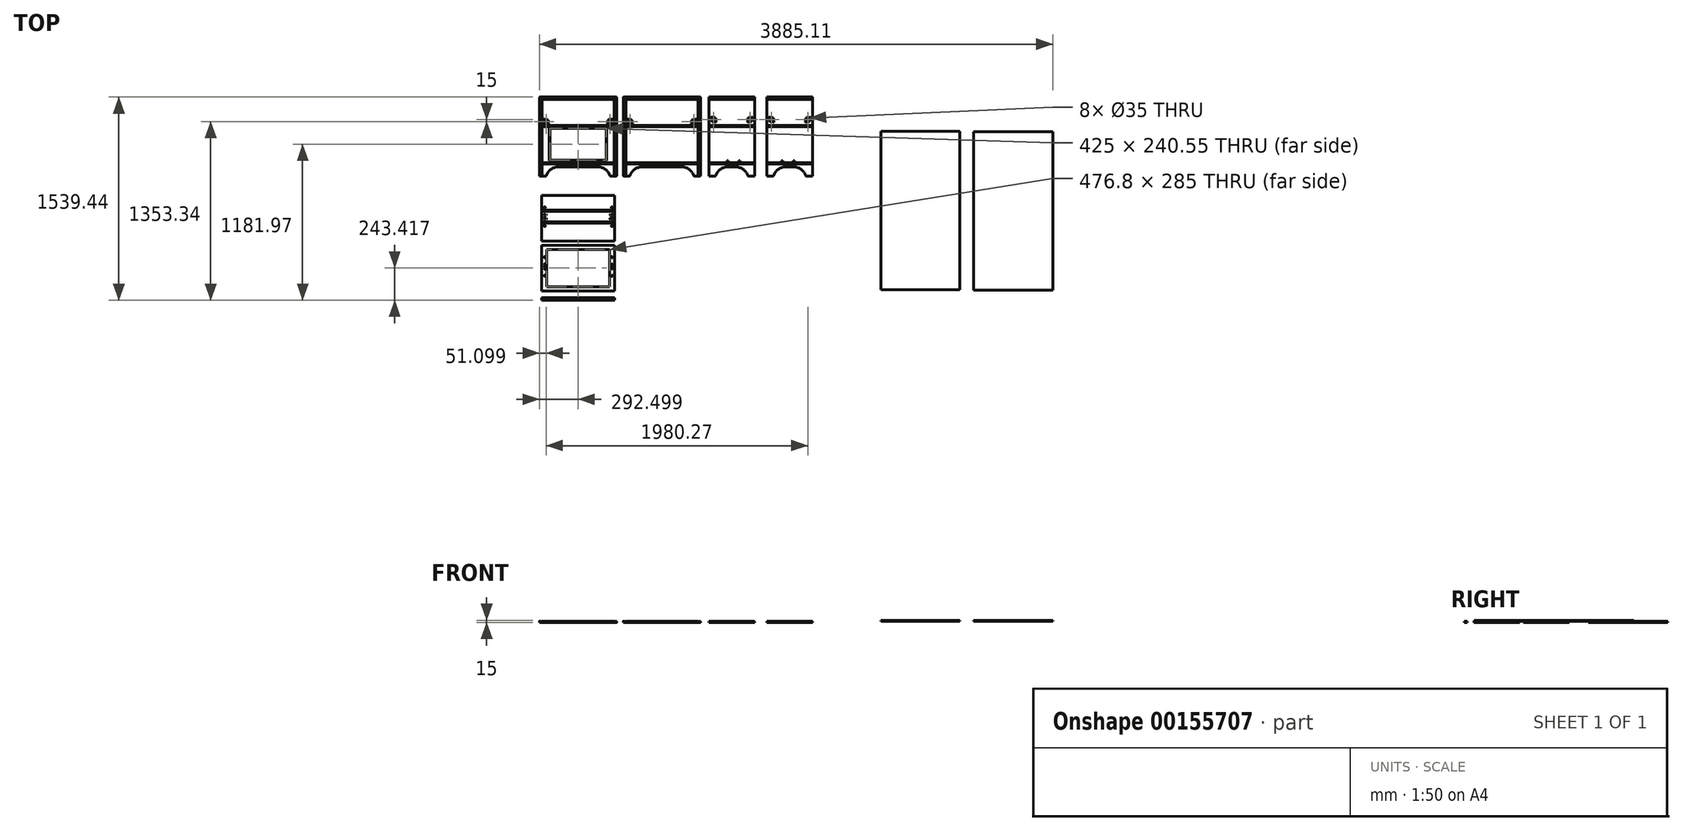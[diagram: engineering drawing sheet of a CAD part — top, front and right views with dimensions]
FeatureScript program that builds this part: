
annotation { "Feature Type Name" : "Feature", "Feature Type Description" : "" }
export const myFeature = defineFeature(function(context is Context, id is Id, definition is map)
    precondition{}
    {
        {
            var Q0;
            Q0=qCreatedBy(makeId("Top.planeOp"),FACE);
            var sketch = newSketch(context, id + "F0", { "sketchPlane" : qUnion([Q0])});
            skLineSegment(sketch, "E0", {"start": v(-123.83, 435.25) * mm, "end": v(-123.83, 505.5) * mm});
            skLineSegment(sketch, "E1", {"start": v(-123.83, 505.5) * mm, "end": v(361.17, 505.5) * mm});
            skLineSegment(sketch, "E2", {"start": v(361.17, 505.5) * mm, "end": v(361.17, 435.25) * mm});
            skLineSegment(sketch, "E3", {"start": v(361.17, 435.25) * mm, "end": v(411.17, 435.25) * mm});
            skLineSegment(sketch, "E4", {"start": v(-173.83, 435.25) * mm, "end": v(-123.83, 435.25) * mm});
            skLineSegment(sketch, "E5", {"start": v(-173.83, 435.25) * mm, "end": v(-173.83, 1035.25) * mm});
            skLineSegment(sketch, "E6", {"start": v(-173.83, 1035.25) * mm, "end": v(411.17, 1035.25) * mm});
            skLineSegment(sketch, "E7", {"start": v(411.17, 1035.25) * mm, "end": v(411.17, 435.25) * mm});
            skLineSegment(sketch, "E8", {"start": v(460.22, 1035.25) * mm, "end": v(1045.22, 1035.25) * mm});
            skLineSegment(sketch, "E9", {"start": v(1045.22, 1035.25) * mm, "end": v(1045.22, 435.25) * mm});
            skLineSegment(sketch, "E10", {"start": v(1045.22, 435.25) * mm, "end": v(995.22, 435.25) * mm});
            skLineSegment(sketch, "E11", {"start": v(995.22, 435.25) * mm, "end": v(995.22, 505.5) * mm});
            skLineSegment(sketch, "E12", {"start": v(995.22, 505.5) * mm, "end": v(510.22, 505.5) * mm});
            skLineSegment(sketch, "E13", {"start": v(510.22, 505.5) * mm, "end": v(510.22, 435.25) * mm});
            skLineSegment(sketch, "E14", {"start": v(510.22, 435.25) * mm, "end": v(460.22, 435.25) * mm});
            skLineSegment(sketch, "E15", {"start": v(460.22, 435.25) * mm, "end": v(460.22, 1035.25) * mm});
            skLineSegment(sketch, "E16", {"start": v(118.67, 1035.25) * mm, "end": v(118.67, 876.87) * mm, "construction": true});
            skLineSegment(sketch, "E17", {"start": v(118.67, 876.87) * mm, "end": v(118.67, 826.87) * mm, "construction": true});
            skLineSegment(sketch, "E18", {"start": v(118.67, 826.87) * mm, "end": v(118.67, 798.05) * mm, "construction": true});
            skLineSegment(sketch, "E19", {"start": v(118.67, 798.05) * mm, "end": v(118.67, 557.5) * mm, "construction": true});
            skLineSegment(sketch, "E20", {"start": v(118.67, 557.5) * mm, "end": v(118.67, 505.5) * mm, "construction": true});
            skLineSegment(sketch, "E21.bottom", {"start": v(26.17, 876.87) * mm, "end": v(211.17, 876.87) * mm});
            skLineSegment(sketch, "E21.top", {"start": v(26.17, 826.87) * mm, "end": v(211.17, 826.87) * mm});
            skLineSegment(sketch, "E21.left", {"start": v(26.17, 876.87) * mm, "end": v(26.17, 826.87) * mm});
            skLineSegment(sketch, "E21.right", {"start": v(211.17, 876.87) * mm, "end": v(211.17, 826.87) * mm});
            skLineSegment(sketch, "E22.bottom", {"start": v(-93.83, 798.05) * mm, "end": v(331.17, 798.05) * mm});
            skLineSegment(sketch, "E22.top", {"start": v(-93.83, 557.5) * mm, "end": v(331.17, 557.5) * mm});
            skLineSegment(sketch, "E22.left", {"start": v(-93.83, 798.05) * mm, "end": v(-93.83, 557.5) * mm});
            skLineSegment(sketch, "E22.right", {"start": v(331.17, 798.05) * mm, "end": v(331.17, 557.5) * mm});
            skLineSegment(sketch, "E23", {"start": v(26.17, 851.87) * mm, "end": v(-173.83, 851.87) * mm, "construction": true});
            skLineSegment(sketch, "E24", {"start": v(-93.83, 677.78) * mm, "end": v(-173.83, 677.78) * mm, "construction": true});
            skLineSegment(sketch, "E25", {"start": v(1109.16, 1035.25) * mm, "end": v(1454.16, 1035.25) * mm});
            skLineSegment(sketch, "E26", {"start": v(1454.16, 1035.25) * mm, "end": v(1454.16, 435.25) * mm});
            skLineSegment(sketch, "E27", {"start": v(1454.16, 435.25) * mm, "end": v(1404.16, 435.25) * mm});
            skLineSegment(sketch, "E28", {"start": v(1404.16, 435.25) * mm, "end": v(1404.16, 505.5) * mm});
            skLineSegment(sketch, "E29", {"start": v(1404.16, 505.5) * mm, "end": v(1159.16, 505.5) * mm});
            skLineSegment(sketch, "E30", {"start": v(1159.16, 505.5) * mm, "end": v(1159.16, 435.25) * mm});
            skLineSegment(sketch, "E31", {"start": v(1159.16, 435.25) * mm, "end": v(1109.16, 435.25) * mm});
            skLineSegment(sketch, "E32", {"start": v(1109.16, 435.25) * mm, "end": v(1109.16, 1035.25) * mm});
            skLineSegment(sketch, "E33", {"start": v(-163.83, 435.25) * mm, "end": v(-163.83, 1035.25) * mm});
            skLineSegment(sketch, "E34", {"start": v(-154.73, 435.25) * mm, "end": v(-154.73, 1035.25) * mm});
            skLineSegment(sketch, "E35", {"start": v(401.17, 435.25) * mm, "end": v(401.17, 1035.25) * mm});
            skLineSegment(sketch, "E36", {"start": v(392.07, 435.25) * mm, "end": v(392.07, 1035.25) * mm});
            skLineSegment(sketch, "E37", {"start": v(-154.73, 905.25) * mm, "end": v(392.07, 905.25) * mm});
            skLineSegment(sketch, "E38", {"start": v(392.07, 896.15) * mm, "end": v(-154.73, 896.15) * mm});
            skLineSegment(sketch, "E39", {"start": v(-154.73, 820.15) * mm, "end": v(392.07, 820.15) * mm});
            skLineSegment(sketch, "E40", {"start": v(392.07, 811.05) * mm, "end": v(-154.73, 811.05) * mm});
            skLineSegment(sketch, "E41", {"start": v(-154.73, 536.05) * mm, "end": v(392.07, 536.05) * mm});
            skLineSegment(sketch, "E42", {"start": v(392.07, 526.95) * mm, "end": v(-154.73, 526.95) * mm});
            skLineSegment(sketch, "E43", {"start": v(71.2, 905.25) * mm, "end": v(71.2, 1035.25) * mm, "construction": true});
            skLineSegment(sketch, "E44", {"start": v(71.36, 811.05) * mm, "end": v(71.36, 798.05) * mm, "construction": true});
            skLineSegment(sketch, "E45", {"start": v(27.92, 557.5) * mm, "end": v(27.92, 536.05) * mm, "construction": true});
            skLineSegment(sketch, "E46", {"start": v(29.17, 526.95) * mm, "end": v(29.17, 505.5) * mm, "construction": true});
            skLineSegment(sketch, "E47", {"start": v(470.22, 435.25) * mm, "end": v(470.22, 1035.25) * mm});
            skLineSegment(sketch, "E48", {"start": v(479.32, 435.25) * mm, "end": v(479.32, 1035.25) * mm});
            skLineSegment(sketch, "E49", {"start": v(1026.12, 435.25) * mm, "end": v(1026.12, 1035.25) * mm});
            skLineSegment(sketch, "E50", {"start": v(1035.22, 435.25) * mm, "end": v(1035.22, 1035.25) * mm});
            skLineSegment(sketch, "E51", {"start": v(479.32, 905.25) * mm, "end": v(1026.12, 905.25) * mm});
            skLineSegment(sketch, "E52", {"start": v(1026.12, 896.15) * mm, "end": v(479.32, 896.15) * mm});
            skLineSegment(sketch, "E53", {"start": v(479.32, 820.15) * mm, "end": v(1026.12, 820.15) * mm});
            skLineSegment(sketch, "E54", {"start": v(1026.12, 811.05) * mm, "end": v(479.32, 811.05) * mm});
            skLineSegment(sketch, "E55", {"start": v(479.32, 536.05) * mm, "end": v(1026.12, 536.05) * mm});
            skLineSegment(sketch, "E56", {"start": v(1026.12, 526.95) * mm, "end": v(479.32, 526.95) * mm});
            skLineSegment(sketch, "E57", {"start": v(-1640.99, 1035.25) * mm, "end": v(2090.02, 1035.25) * mm, "construction": true});
            skLineSegment(sketch, "E58", {"start": v(2090.02, 820.15) * mm, "end": v(-1631.04, 820.15) * mm, "construction": true});
            skLineSegment(sketch, "E59", {"start": v(-1631.04, 536.05) * mm, "end": v(2077.59, 536.05) * mm, "construction": true});
            skLineSegment(sketch, "E60", {"start": v(-795.13, 905.25) * mm, "end": v(2085.73, 905.25) * mm, "construction": true});
            skLineSegment(sketch, "E61", {"start": v(-1656.92, 811.05) * mm, "end": v(2077.22, 811.05) * mm, "construction": true});
            skLineSegment(sketch, "E62", {"start": v(2079.96, 526.95) * mm, "end": v(-1667.36, 526.95) * mm, "construction": true});
            skLineSegment(sketch, "E63", {"start": v(-1685.91, 896.15) * mm, "end": v(2079.86, 896.15) * mm, "construction": true});
            skLineSegment(sketch, "E64", {"start": v(1109.16, 536.05) * mm, "end": v(1454.16, 536.05) * mm});
            skLineSegment(sketch, "E65", {"start": v(1454.16, 526.95) * mm, "end": v(1109.16, 526.95) * mm});
            skLineSegment(sketch, "E66", {"start": v(1109.16, 820.15) * mm, "end": v(1454.16, 820.15) * mm});
            skLineSegment(sketch, "E67", {"start": v(1454.16, 811.05) * mm, "end": v(1109.16, 811.05) * mm});
            skLineSegment(sketch, "E68", {"start": v(1109.16, 905.25) * mm, "end": v(1454.16, 905.25) * mm});
            skLineSegment(sketch, "E69", {"start": v(1454.16, 896.15) * mm, "end": v(1109.16, 896.15) * mm});
            skLineSegment(sketch, "E70", {"start": v(-157.73, 320.51) * mm, "end": v(-157.73, -755.2) * mm, "construction": true});
            skLineSegment(sketch, "E71", {"start": v(395.07, 320.51) * mm, "end": v(395.07, -1181.01) * mm, "construction": true});
            skLineSegment(sketch, "E72.bottom", {"start": v(-157.73, 288.42) * mm, "end": v(395.07, 288.42) * mm});
            skLineSegment(sketch, "E72.top", {"start": v(-157.73, -56.58) * mm, "end": v(395.07, -56.58) * mm});
            skLineSegment(sketch, "E72.left", {"start": v(-157.73, 288.42) * mm, "end": v(-157.73, -56.58) * mm});
            skLineSegment(sketch, "E72.right", {"start": v(395.07, 288.42) * mm, "end": v(395.07, -56.58) * mm});
            skLineSegment(sketch, "E73.bottom", {"start": v(-157.73, -88.27) * mm, "end": v(395.07, -88.27) * mm});
            skLineSegment(sketch, "E73.top", {"start": v(-157.73, -433.27) * mm, "end": v(395.07, -433.27) * mm});
            skLineSegment(sketch, "E73.left", {"start": v(-157.73, -88.27) * mm, "end": v(-157.73, -433.27) * mm});
            skLineSegment(sketch, "E73.right", {"start": v(395.07, -88.27) * mm, "end": v(395.07, -433.27) * mm});
            skLineSegment(sketch, "E74.bottom", {"start": v(-119.73, -118.27) * mm, "end": v(357.07, -118.27) * mm});
            skLineSegment(sketch, "E74.top", {"start": v(-119.73, -403.27) * mm, "end": v(357.07, -403.27) * mm});
            skLineSegment(sketch, "E74.left", {"start": v(-119.73, -118.27) * mm, "end": v(-119.73, -403.27) * mm});
            skLineSegment(sketch, "E74.right", {"start": v(357.07, -118.27) * mm, "end": v(357.07, -403.27) * mm});
            skLineSegment(sketch, "E75", {"start": v(-157.73, -260.77) * mm, "end": v(-119.73, -260.77) * mm, "construction": true});
            skLineSegment(sketch, "E76", {"start": v(118.67, -88.27) * mm, "end": v(118.67, -118.27) * mm, "construction": true});
            skLineSegment(sketch, "E77", {"start": v(395.07, -260.77) * mm, "end": v(357.07, -260.77) * mm, "construction": true});
            skLineSegment(sketch, "E78", {"start": v(118.67, -433.27) * mm, "end": v(118.67, -403.27) * mm, "construction": true});
            skLineSegment(sketch, "E79", {"start": v(-154.73, 435.25) * mm, "end": v(-154.73, 320.51) * mm, "construction": true});
            skLineSegment(sketch, "E80", {"start": v(-154.73, 320.51) * mm, "end": v(392.07, 320.51) * mm, "construction": true});
            skLineSegment(sketch, "E81", {"start": v(392.07, 320.51) * mm, "end": v(392.07, 435.25) * mm, "construction": true});
            skLineSegment(sketch, "E82", {"start": v(-154.73, 320.51) * mm, "end": v(-157.73, 320.51) * mm, "construction": true});
            skLineSegment(sketch, "E83", {"start": v(392.07, 320.51) * mm, "end": v(395.07, 320.51) * mm, "construction": true});
            skPoint(sketch, "E84.startSnap0", {"position": v(118.67, -118.27) * mm});
            skCircle(sketch, "E85", {"center": v(132.27, 128.42) * mm, "radius": 27.3 * mm});
            skLineSegment(sketch, "E86", {"start": v(132.27, 128.42) * mm, "end": v(-157.73, 128.42) * mm, "construction": true});
            skLineSegment(sketch, "E87", {"start": v(132.27, 128.42) * mm, "end": v(132.27, -56.58) * mm, "construction": true});
            skLineSegment(sketch, "E88", {"start": v(-368.37, 1025.25) * mm, "end": v(2135.5, 1025.25) * mm, "construction": true});
            skLineSegment(sketch, "E89", {"start": v(2105.89, 1016.15) * mm, "end": v(-364.93, 1016.15) * mm, "construction": true});
            skLineSegment(sketch, "E90", {"start": v(-154.73, 1025.25) * mm, "end": v(392.07, 1025.25) * mm});
            skLineSegment(sketch, "E91", {"start": v(392.07, 1016.15) * mm, "end": v(-154.73, 1016.15) * mm});
            skLineSegment(sketch, "E92", {"start": v(479.32, 1025.25) * mm, "end": v(1026.12, 1025.25) * mm});
            skLineSegment(sketch, "E93", {"start": v(1026.12, 1016.15) * mm, "end": v(479.32, 1016.15) * mm});
            skLineSegment(sketch, "E94", {"start": v(1109.16, 1025.25) * mm, "end": v(1454.16, 1025.25) * mm});
            skLineSegment(sketch, "E95", {"start": v(1454.16, 1016.15) * mm, "end": v(1109.16, 1016.15) * mm});
            skLineSegment(sketch, "E96.bottom", {"start": v(-98.83, 803.05) * mm, "end": v(336.17, 803.05) * mm});
            skLineSegment(sketch, "E96.top", {"start": v(-98.83, 552.5) * mm, "end": v(336.17, 552.5) * mm});
            skLineSegment(sketch, "E96.left", {"start": v(-98.83, 803.05) * mm, "end": v(-98.83, 552.5) * mm});
            skLineSegment(sketch, "E96.right", {"start": v(336.17, 803.05) * mm, "end": v(336.17, 552.5) * mm});
            skLineSegment(sketch, "E97", {"start": v(331.17, 798.05) * mm, "end": v(336.17, 803.05) * mm, "construction": true});
            skLineSegment(sketch, "E98", {"start": v(331.17, 557.5) * mm, "end": v(336.17, 552.5) * mm, "construction": true});
            skLineSegment(sketch, "E99", {"start": v(-93.83, 557.5) * mm, "end": v(-98.83, 552.5) * mm, "construction": true});
            skLineSegment(sketch, "E100", {"start": v(-93.83, 798.05) * mm, "end": v(-98.83, 803.05) * mm, "construction": true});
            skLineSegment(sketch, "E101", {"start": v(92.3, 798.05) * mm, "end": v(92.3, 803.05) * mm, "construction": true});
            skLineSegment(sketch, "E102", {"start": v(-84.43, 128.42) * mm, "end": v(-84.43, 168.42) * mm, "construction": true});
            skLineSegment(sketch, "E103", {"start": v(-84.43, 128.42) * mm, "end": v(-84.43, 88.42) * mm, "construction": true});
            skLineSegment(sketch, "E104", {"start": v(-157.73, 168.42) * mm, "end": v(395.07, 168.42) * mm});
            skLineSegment(sketch, "E105", {"start": v(-157.73, 88.42) * mm, "end": v(395.07, 88.42) * mm});
            skLineSegment(sketch, "E106", {"start": v(-157.73, 177.52) * mm, "end": v(395.07, 177.52) * mm});
            skLineSegment(sketch, "E107", {"start": v(-157.73, 79.32) * mm, "end": v(395.07, 79.32) * mm});
            skLineSegment(sketch, "E108", {"start": v(-157.73, -484.19) * mm, "end": v(395.07, -484.19) * mm});
            skLineSegment(sketch, "E109", {"start": v(-157.73, -484.19) * mm, "end": v(-157.73, -504.19) * mm});
            skLineSegment(sketch, "E110", {"start": v(-157.73, -504.19) * mm, "end": v(395.07, -504.19) * mm});
            skLineSegment(sketch, "E111", {"start": v(395.07, -504.19) * mm, "end": v(395.07, -484.19) * mm});
            skLineSegment(sketch, "E112", {"start": v(1294.16, 573.28) * mm, "end": v(1254.16, 573.28) * mm, "construction": true});
            skLineSegment(sketch, "E113", {"start": v(1294.16, 573.28) * mm, "end": v(1334.16, 573.28) * mm, "construction": true});
            skLineSegment(sketch, "E114", {"start": v(1254.16, 573.28) * mm, "end": v(1254.16, 536.05) * mm, "construction": true});
            skLineSegment(sketch, "E115", {"start": v(1334.16, 573.28) * mm, "end": v(1334.16, 536.05) * mm, "construction": true});
            skLineSegment(sketch, "E116", {"start": v(1254.16, 553.15) * mm, "end": v(1245.06, 553.15) * mm});
            skLineSegment(sketch, "E117", {"start": v(1245.06, 553.15) * mm, "end": v(1245.06, 536.05) * mm});
            skLineSegment(sketch, "E118", {"start": v(1254.16, 553.15) * mm, "end": v(1254.16, 536.05) * mm});
            skLineSegment(sketch, "E119", {"start": v(1334.16, 553.15) * mm, "end": v(1343.26, 553.15) * mm});
            skLineSegment(sketch, "E120", {"start": v(1343.26, 553.15) * mm, "end": v(1343.26, 536.05) * mm});
            skLineSegment(sketch, "E121", {"start": v(1334.16, 553.15) * mm, "end": v(1334.16, 536.05) * mm});
            skLineSegment(sketch, "E122", {"start": v(1294.16, 573.28) * mm, "end": v(1294.16, 536.05) * mm, "construction": true});
            skLineSegment(sketch, "E123", {"start": v(1294.16, 573.28) * mm, "end": v(1454.16, 573.28) * mm, "construction": true});
            skLineSegment(sketch, "E124", {"start": v(1294.16, 573.28) * mm, "end": v(1109.16, 573.28) * mm, "construction": true});
            skLineSegment(sketch, "E125", {"start": v(1547.54, 1035.25) * mm, "end": v(1892.54, 1035.25) * mm});
            skLineSegment(sketch, "E126", {"start": v(1892.54, 1035.25) * mm, "end": v(1892.54, 435.25) * mm});
            skLineSegment(sketch, "E127", {"start": v(1892.54, 435.25) * mm, "end": v(1842.54, 435.25) * mm});
            skLineSegment(sketch, "E128", {"start": v(1842.54, 435.25) * mm, "end": v(1842.54, 505.5) * mm});
            skLineSegment(sketch, "E129", {"start": v(1842.54, 505.5) * mm, "end": v(1597.54, 505.5) * mm});
            skLineSegment(sketch, "E130", {"start": v(1597.54, 505.5) * mm, "end": v(1597.54, 435.25) * mm});
            skLineSegment(sketch, "E131", {"start": v(1597.54, 435.25) * mm, "end": v(1547.54, 435.25) * mm});
            skLineSegment(sketch, "E132", {"start": v(1547.54, 435.25) * mm, "end": v(1547.54, 1035.25) * mm});
            skLineSegment(sketch, "E133", {"start": v(1547.54, 536.05) * mm, "end": v(1892.54, 536.05) * mm});
            skLineSegment(sketch, "E134", {"start": v(1892.54, 526.95) * mm, "end": v(1547.54, 526.95) * mm});
            skLineSegment(sketch, "E135", {"start": v(1547.54, 820.15) * mm, "end": v(1892.54, 820.15) * mm});
            skLineSegment(sketch, "E136", {"start": v(1892.54, 811.05) * mm, "end": v(1547.54, 811.05) * mm});
            skLineSegment(sketch, "E137", {"start": v(1547.54, 905.25) * mm, "end": v(1892.54, 905.25) * mm});
            skLineSegment(sketch, "E138", {"start": v(1892.54, 896.15) * mm, "end": v(1547.54, 896.15) * mm});
            skLineSegment(sketch, "E139", {"start": v(1547.54, 1025.25) * mm, "end": v(1892.54, 1025.25) * mm});
            skLineSegment(sketch, "E140", {"start": v(1892.54, 1016.15) * mm, "end": v(1547.54, 1016.15) * mm});
            skLineSegment(sketch, "E141", {"start": v(1707.54, 567.75) * mm, "end": v(1667.54, 567.75) * mm, "construction": true});
            skLineSegment(sketch, "E142", {"start": v(1707.54, 567.75) * mm, "end": v(1747.54, 567.75) * mm, "construction": true});
            skLineSegment(sketch, "E143", {"start": v(1667.54, 567.75) * mm, "end": v(1667.54, 536.05) * mm, "construction": true});
            skLineSegment(sketch, "E144", {"start": v(1747.54, 567.75) * mm, "end": v(1747.54, 536.05) * mm, "construction": true});
            skLineSegment(sketch, "E145", {"start": v(1667.54, 553.15) * mm, "end": v(1658.44, 553.15) * mm});
            skLineSegment(sketch, "E146", {"start": v(1658.44, 553.15) * mm, "end": v(1658.44, 536.05) * mm});
            skLineSegment(sketch, "E147", {"start": v(1667.54, 553.15) * mm, "end": v(1667.54, 536.05) * mm});
            skLineSegment(sketch, "E148", {"start": v(1747.54, 553.15) * mm, "end": v(1756.64, 553.15) * mm});
            skLineSegment(sketch, "E149", {"start": v(1756.64, 553.15) * mm, "end": v(1756.64, 536.05) * mm});
            skLineSegment(sketch, "E150", {"start": v(1747.54, 553.15) * mm, "end": v(1747.54, 536.05) * mm});
            skLineSegment(sketch, "E151", {"start": v(1707.54, 567.75) * mm, "end": v(1707.54, 536.05) * mm, "construction": true});
            skLineSegment(sketch, "E152", {"start": v(1707.54, 567.75) * mm, "end": v(1892.54, 567.75) * mm, "construction": true});
            skLineSegment(sketch, "E153", {"start": v(1707.54, 567.75) * mm, "end": v(1547.54, 567.75) * mm, "construction": true});
            skSolve(sketch);
        }
        {
            var Q0;
            {var subQ0=sQuery(id+"F0.wireOp",EDGE,"E54");Q0=makeQuery(id+"F0.imprint","IMPRINT",FACE,{"disambiguationData":[TD([[makeQuery(id+"F0.imprint","IMPRINT",EDGE,{"derivedFrom":subQ0}),1.0]])]});}
            var Q1;
            Q1=makeQuery(id+"F0.imprint","IMPRINT",FACE,{"disambiguationData":[TD([[makeQuery(id+"F0.imprint","IMPRINT",EDGE,{"derivedFrom":sQuery(id+"F0.wireOp",EDGE,"E22.top")}),-1.0]])]});
            var Q2;
            {var subQ0=sQuery(id+"F0.wireOp",EDGE,"E9");Q2=makeQuery(id+"F0.imprint","IMPRINT",FACE,{"disambiguationData":[TD([[makeQuery(id+"F0.imprint","IMPRINT",EDGE,{"derivedFrom":subQ0}),-1.0]])]});}
            var Q3;
            {var subQ0=sQuery(id+"F0.wireOp",EDGE,"E51");Q3=makeQuery(id+"F0.imprint","IMPRINT",FACE,{"disambiguationData":[TD([[makeQuery(id+"F0.imprint","IMPRINT",EDGE,{"derivedFrom":subQ0}),1.0]])]});}
            var Q4;
            {var subQ0=sQuery(id+"F0.wireOp",EDGE,"E66");Q4=makeQuery(id+"F0.imprint","IMPRINT",FACE,{"disambiguationData":[TD([[makeQuery(id+"F0.imprint","IMPRINT",EDGE,{"derivedFrom":subQ0}),1.0]])]});}
            var Q5;
            Q5=makeQuery(id+"F0.imprint","IMPRINT",FACE,{"disambiguationData":[TD([[makeQuery(id+"F0.imprint","IMPRINT",EDGE,{"derivedFrom":sQuery(id+"F0.wireOp",EDGE,"E73.bottom")}),-1.0]])]});
            var Q6;
            {var subQ0=sQuery(id+"F0.wireOp",EDGE,"E27");Q6=makeQuery(id+"F0.imprint","IMPRINT",FACE,{"disambiguationData":[TD([[makeQuery(id+"F0.imprint","IMPRINT",EDGE,{"derivedFrom":subQ0}),-1.0]])]});}
            var Q7;
            {var subQ0=sQuery(id+"F0.wireOp",EDGE,"E25");Q7=makeQuery(id+"F0.imprint","IMPRINT",FACE,{"disambiguationData":[TD([[makeQuery(id+"F0.imprint","IMPRINT",EDGE,{"derivedFrom":subQ0}),-1.0]])]});}
            var Q8;
            {var subQ0=sQuery(id+"F0.wireOp",EDGE,"E72.bottom");Q8=makeQuery(id+"F0.imprint","IMPRINT",FACE,{"disambiguationData":[TD([[makeQuery(id+"F0.imprint","IMPRINT",EDGE,{"derivedFrom":subQ0}),-1.0]])]});}
            var Q9;
            {var subQ0=sQuery(id+"F0.wireOp",EDGE,"E37");Q9=makeQuery(id+"F0.imprint","IMPRINT",FACE,{"disambiguationData":[TD([[makeQuery(id+"F0.imprint","IMPRINT",EDGE,{"derivedFrom":subQ0}),1.0]])]});}
            var Q10;
            {var subQ6=sQuery(id+"F0.wireOp",EDGE,"E67");Q10=makeQuery(id+"F0.imprint","IMPRINT",FACE,{"disambiguationData":[TD([[makeQuery(id+"F0.imprint","IMPRINT",EDGE,{"derivedFrom":subQ6}),1.0]])]});}
            var Q11;
            {var subQ6=sQuery(id+"F0.wireOp",EDGE,"E0");Q11=makeQuery(id+"F0.imprint","IMPRINT",FACE,{"disambiguationData":[TD([[makeQuery(id+"F0.imprint","IMPRINT",EDGE,{"derivedFrom":subQ6}),1.0]])]});}
            var Q12;
            {var subQ5=sQuery(id+"F0.wireOp",EDGE,"E21.bottom");Q12=makeQuery(id+"F0.imprint","IMPRINT",FACE,{"disambiguationData":[TD([[makeQuery(id+"F0.imprint","IMPRINT",EDGE,{"derivedFrom":subQ5}),1.0]])]});}
            var Q13;
            {var subQ0=sQuery(id+"F0.wireOp",EDGE,"E52");Q13=makeQuery(id+"F0.imprint","IMPRINT",FACE,{"disambiguationData":[TD([[makeQuery(id+"F0.imprint","IMPRINT",EDGE,{"derivedFrom":subQ0}),1.0]])]});}
            var Q14;
            {var subQ5=sQuery(id+"F0.wireOp",EDGE,"E11");Q14=makeQuery(id+"F0.imprint","IMPRINT",FACE,{"disambiguationData":[TD([[makeQuery(id+"F0.imprint","IMPRINT",EDGE,{"derivedFrom":subQ5}),-1.0]])]});}
            var Q15;
            {var subQ3=sQuery(id+"F0.wireOp",EDGE,"E33");Q15=makeQuery(id+"F0.imprint","IMPRINT",FACE,{"disambiguationData":[TD([[makeQuery(id+"F0.imprint","IMPRINT",EDGE,{"derivedFrom":subQ3}),-1.0]])]});}
            var Q16;
            {var subQ0=sQuery(id+"F0.wireOp",EDGE,"E55");Q16=makeQuery(id+"F0.imprint","IMPRINT",FACE,{"disambiguationData":[TD([[makeQuery(id+"F0.imprint","IMPRINT",EDGE,{"derivedFrom":subQ0}),-1.0]])]});}
            var Q17;
            {var subQ11=sQuery(id+"F0.wireOp",EDGE,"E35");Q17=makeQuery(id+"F0.imprint","IMPRINT",FACE,{"disambiguationData":[TD([[makeQuery(id+"F0.imprint","IMPRINT",EDGE,{"derivedFrom":subQ11}),1.0]])]});}
            var Q18;
            {var subQ0=sQuery(id+"F0.wireOp",EDGE,"E37");Q18=makeQuery(id+"F0.imprint","IMPRINT",FACE,{"disambiguationData":[TD([[makeQuery(id+"F0.imprint","IMPRINT",EDGE,{"derivedFrom":subQ0}),-1.0]])]});}
            var Q19;
            {var subQ0=sQuery(id+"F0.wireOp",EDGE,"E66");Q19=makeQuery(id+"F0.imprint","IMPRINT",FACE,{"disambiguationData":[TD([[makeQuery(id+"F0.imprint","IMPRINT",EDGE,{"derivedFrom":subQ0}),-1.0]])]});}
            var Q20;
            {var subQ0=sQuery(id+"F0.wireOp",EDGE,"E68");Q20=makeQuery(id+"F0.imprint","IMPRINT",FACE,{"disambiguationData":[TD([[makeQuery(id+"F0.imprint","IMPRINT",EDGE,{"derivedFrom":subQ0}),-1.0]])]});}
            var Q21;
            {var subQ0=sQuery(id+"F0.wireOp",EDGE,"E15");Q21=makeQuery(id+"F0.imprint","IMPRINT",FACE,{"disambiguationData":[TD([[makeQuery(id+"F0.imprint","IMPRINT",EDGE,{"derivedFrom":subQ0}),-1.0]])]});}
            var Q22;
            {var subQ0=sQuery(id+"F0.wireOp",EDGE,"E5");Q22=makeQuery(id+"F0.imprint","IMPRINT",FACE,{"disambiguationData":[TD([[makeQuery(id+"F0.imprint","IMPRINT",EDGE,{"derivedFrom":subQ0}),-1.0]])]});}
            var Q23;
            {var subQ0=sQuery(id+"F0.wireOp",EDGE,"E7");Q23=makeQuery(id+"F0.imprint","IMPRINT",FACE,{"disambiguationData":[TD([[makeQuery(id+"F0.imprint","IMPRINT",EDGE,{"derivedFrom":subQ0}),-1.0]])]});}
            var Q24;
            {var subQ5=sQuery(id+"F0.wireOp",EDGE,"E65");Q24=makeQuery(id+"F0.imprint","IMPRINT",FACE,{"disambiguationData":[TD([[makeQuery(id+"F0.imprint","IMPRINT",EDGE,{"derivedFrom":subQ5}),-1.0]])]});}
            var Q25;
            {var subQ0=sQuery(id+"F0.wireOp",EDGE,"E39");var subQ1=sQuery(id+"F0.wireOp",EDGE,"E21.left");var subQ2=makeQuery(id+"F0.imprint","INTERSECT",VERTEX,{"derivedFrom":[subQ1,subQ0]});Q25=makeQuery(id+"F0.imprint","IMPRINT",FACE,{"disambiguationData":[TD([[makeQuery(id+"F0.imprint","IMPRINT",EDGE,{"disambiguationData":[TD([[subQ2,-1.0]])],"derivedFrom":subQ1}),1.0]])]});}
            var Q26;
            {var subQ0=sQuery(id+"F0.wireOp",EDGE,"E39");var subQ1=sQuery(id+"F0.wireOp",EDGE,"E21.left");var subQ2=makeQuery(id+"F0.imprint","INTERSECT",VERTEX,{"derivedFrom":[subQ1,subQ0]});Q26=makeQuery(id+"F0.imprint","IMPRINT",FACE,{"disambiguationData":[TD([[makeQuery(id+"F0.imprint","IMPRINT",EDGE,{"disambiguationData":[TD([[subQ2,-1.0]])],"derivedFrom":subQ1}),-1.0]])]});}
            var Q27;
            {var subQ0=sQuery(id+"F0.wireOp",EDGE,"E39");var subQ1=sQuery(id+"F0.wireOp",EDGE,"E21.right");var subQ2=makeQuery(id+"F0.imprint","INTERSECT",VERTEX,{"derivedFrom":[subQ1,subQ0]});Q27=makeQuery(id+"F0.imprint","IMPRINT",FACE,{"disambiguationData":[TD([[makeQuery(id+"F0.imprint","IMPRINT",EDGE,{"disambiguationData":[TD([[subQ2,-1.0]])],"derivedFrom":subQ1}),1.0]])]});}
            var Q28;
            {var subQ0=sQuery(id+"F0.wireOp",EDGE,"E51");Q28=makeQuery(id+"F0.imprint","IMPRINT",FACE,{"disambiguationData":[TD([[makeQuery(id+"F0.imprint","IMPRINT",EDGE,{"derivedFrom":subQ0}),-1.0]])]});}
            var Q29;
            {var subQ0=sQuery(id+"F0.wireOp",EDGE,"E41");Q29=makeQuery(id+"F0.imprint","IMPRINT",FACE,{"disambiguationData":[TD([[makeQuery(id+"F0.imprint","IMPRINT",EDGE,{"derivedFrom":subQ0}),-1.0]])]});}
            var Q30;
            {var subQ0=sQuery(id+"F0.wireOp",EDGE,"E53");Q30=makeQuery(id+"F0.imprint","IMPRINT",FACE,{"disambiguationData":[TD([[makeQuery(id+"F0.imprint","IMPRINT",EDGE,{"derivedFrom":subQ0}),-1.0]])]});}
            var Q31;
            {var subQ11=sQuery(id+"F0.wireOp",EDGE,"E47");Q31=makeQuery(id+"F0.imprint","IMPRINT",FACE,{"disambiguationData":[TD([[makeQuery(id+"F0.imprint","IMPRINT",EDGE,{"derivedFrom":subQ11}),-1.0]])]});}
            var Q32;
            {var subQ5=sQuery(id+"F0.wireOp",EDGE,"E50");Q32=makeQuery(id+"F0.imprint","IMPRINT",FACE,{"disambiguationData":[TD([[makeQuery(id+"F0.imprint","IMPRINT",EDGE,{"derivedFrom":subQ5}),1.0]])]});}
            var Q33;
            {var subQ0=sQuery(id+"F0.wireOp",EDGE,"E90");Q33=makeQuery(id+"F0.imprint","IMPRINT",FACE,{"disambiguationData":[TD([[makeQuery(id+"F0.imprint","IMPRINT",EDGE,{"derivedFrom":subQ0}),-1.0]])]});}
            var Q34;
            {var subQ5=sQuery(id+"F0.wireOp",EDGE,"E90");Q34=makeQuery(id+"F0.imprint","IMPRINT",FACE,{"disambiguationData":[TD([[makeQuery(id+"F0.imprint","IMPRINT",EDGE,{"derivedFrom":subQ5}),1.0]])]});}
            var Q35;
            {var subQ5=sQuery(id+"F0.wireOp",EDGE,"E92");Q35=makeQuery(id+"F0.imprint","IMPRINT",FACE,{"disambiguationData":[TD([[makeQuery(id+"F0.imprint","IMPRINT",EDGE,{"derivedFrom":subQ5}),1.0]])]});}
            var Q36;
            {var subQ0=sQuery(id+"F0.wireOp",EDGE,"E92");Q36=makeQuery(id+"F0.imprint","IMPRINT",FACE,{"disambiguationData":[TD([[makeQuery(id+"F0.imprint","IMPRINT",EDGE,{"derivedFrom":subQ0}),-1.0]])]});}
            var Q37;
            {var subQ0=sQuery(id+"F0.wireOp",EDGE,"E94");Q37=makeQuery(id+"F0.imprint","IMPRINT",FACE,{"disambiguationData":[TD([[makeQuery(id+"F0.imprint","IMPRINT",EDGE,{"derivedFrom":subQ0}),-1.0]])]});}
            var Q38;
            {var subQ0=sQuery(id+"F0.wireOp",EDGE,"E68");Q38=makeQuery(id+"F0.imprint","IMPRINT",FACE,{"disambiguationData":[TD([[makeQuery(id+"F0.imprint","IMPRINT",EDGE,{"derivedFrom":subQ0}),1.0]])]});}
            var Q39;
            {var subQ0=sQuery(id+"F0.wireOp",EDGE,"E21.bottom");Q39=makeQuery(id+"F0.imprint","IMPRINT",FACE,{"disambiguationData":[TD([[makeQuery(id+"F0.imprint","IMPRINT",EDGE,{"derivedFrom":subQ0}),-1.0]])]});}
            var Q40;
            {var subQ7=sQuery(id+"F0.wireOp",EDGE,"E41");Q40=makeQuery(id+"F0.imprint","IMPRINT",FACE,{"disambiguationData":[TD([[makeQuery(id+"F0.imprint","IMPRINT",EDGE,{"derivedFrom":subQ7}),1.0]])]});}
            var Q41;
            Q41=makeQuery(id+"F0.imprint","IMPRINT",FACE,{"disambiguationData":[TD([[makeQuery(id+"F0.imprint","IMPRINT",EDGE,{"derivedFrom":sQuery(id+"F0.wireOp",EDGE,"E85")}),1.0]])]});
            var Q42;
            Q42=makeQuery(id+"F0.imprint","IMPRINT",FACE,{"disambiguationData":[TD([[makeQuery(id+"F0.imprint","IMPRINT",EDGE,{"derivedFrom":sQuery(id+"F0.wireOp",EDGE,"E85")}),-1.0]])]});
            var Q43;
            {var subQ0=sQuery(id+"F0.wireOp",EDGE,"E72.top");Q43=makeQuery(id+"F0.imprint","IMPRINT",FACE,{"disambiguationData":[TD([[makeQuery(id+"F0.imprint","IMPRINT",EDGE,{"derivedFrom":subQ0}),1.0]])]});}
            var Q44;
            {var subQ0=sQuery(id+"F0.wireOp",EDGE,"E105");Q44=makeQuery(id+"F0.imprint","IMPRINT",FACE,{"disambiguationData":[TD([[makeQuery(id+"F0.imprint","IMPRINT",EDGE,{"derivedFrom":subQ0}),-1.0]])]});}
            var Q45;
            {var subQ0=sQuery(id+"F0.wireOp",EDGE,"E104");Q45=makeQuery(id+"F0.imprint","IMPRINT",FACE,{"disambiguationData":[TD([[makeQuery(id+"F0.imprint","IMPRINT",EDGE,{"derivedFrom":subQ0}),1.0]])]});}
            var Q46;
            Q46=makeQuery(id+"F0.imprint","IMPRINT",FACE,{"disambiguationData":[TD([[makeQuery(id+"F0.imprint","IMPRINT",EDGE,{"derivedFrom":sQuery(id+"F0.wireOp",EDGE,"E116")}),1.0]])]});
            var Q47;
            Q47=makeQuery(id+"F0.imprint","IMPRINT",FACE,{"disambiguationData":[TD([[makeQuery(id+"F0.imprint","IMPRINT",EDGE,{"derivedFrom":sQuery(id+"F0.wireOp",EDGE,"E119")}),-1.0]])]});
            var Q48;
            Q48=makeQuery(id+"F0.imprint","IMPRINT",FACE,{"disambiguationData":[TD([[makeQuery(id+"F0.imprint","IMPRINT",EDGE,{"derivedFrom":sQuery(id+"F0.wireOp",EDGE,"E108")}),-1.0]])]});
            var Q49;
            {var subQ5=sQuery(id+"F0.wireOp",EDGE,"E136");Q49=makeQuery(id+"F0.imprint","IMPRINT",FACE,{"disambiguationData":[TD([[makeQuery(id+"F0.imprint","IMPRINT",EDGE,{"derivedFrom":subQ5}),1.0]])]});}
            var Q50;
            {var subQ0=sQuery(id+"F0.wireOp",EDGE,"E127");Q50=makeQuery(id+"F0.imprint","IMPRINT",FACE,{"disambiguationData":[TD([[makeQuery(id+"F0.imprint","IMPRINT",EDGE,{"derivedFrom":subQ0}),-1.0]])]});}
            var Q51;
            {var subQ0=sQuery(id+"F0.wireOp",EDGE,"E125");Q51=makeQuery(id+"F0.imprint","IMPRINT",FACE,{"disambiguationData":[TD([[makeQuery(id+"F0.imprint","IMPRINT",EDGE,{"derivedFrom":subQ0}),-1.0]])]});}
            var Q52;
            {var subQ0=sQuery(id+"F0.wireOp",EDGE,"E135");Q52=makeQuery(id+"F0.imprint","IMPRINT",FACE,{"disambiguationData":[TD([[makeQuery(id+"F0.imprint","IMPRINT",EDGE,{"derivedFrom":subQ0}),1.0]])]});}
            var Q53;
            {var subQ0=sQuery(id+"F0.wireOp",EDGE,"E137");Q53=makeQuery(id+"F0.imprint","IMPRINT",FACE,{"disambiguationData":[TD([[makeQuery(id+"F0.imprint","IMPRINT",EDGE,{"derivedFrom":subQ0}),1.0]])]});}
            var Q54;
            {var subQ0=sQuery(id+"F0.wireOp",EDGE,"E135");Q54=makeQuery(id+"F0.imprint","IMPRINT",FACE,{"disambiguationData":[TD([[makeQuery(id+"F0.imprint","IMPRINT",EDGE,{"derivedFrom":subQ0}),-1.0]])]});}
            var Q55;
            {var subQ5=sQuery(id+"F0.wireOp",EDGE,"E134");Q55=makeQuery(id+"F0.imprint","IMPRINT",FACE,{"disambiguationData":[TD([[makeQuery(id+"F0.imprint","IMPRINT",EDGE,{"derivedFrom":subQ5}),-1.0]])]});}
            var Q56;
            {var subQ0=sQuery(id+"F0.wireOp",EDGE,"E139");Q56=makeQuery(id+"F0.imprint","IMPRINT",FACE,{"disambiguationData":[TD([[makeQuery(id+"F0.imprint","IMPRINT",EDGE,{"derivedFrom":subQ0}),-1.0]])]});}
            var Q57;
            {var subQ0=sQuery(id+"F0.wireOp",EDGE,"E137");Q57=makeQuery(id+"F0.imprint","IMPRINT",FACE,{"disambiguationData":[TD([[makeQuery(id+"F0.imprint","IMPRINT",EDGE,{"derivedFrom":subQ0}),-1.0]])]});}
            var Q58;
            Q58=makeQuery(id+"F0.imprint","IMPRINT",FACE,{"disambiguationData":[TD([[makeQuery(id+"F0.imprint","IMPRINT",EDGE,{"derivedFrom":sQuery(id+"F0.wireOp",EDGE,"E145")}),1.0]])]});
            var Q59;
            Q59=makeQuery(id+"F0.imprint","IMPRINT",FACE,{"disambiguationData":[TD([[makeQuery(id+"F0.imprint","IMPRINT",EDGE,{"derivedFrom":sQuery(id+"F0.wireOp",EDGE,"E148")}),-1.0]])]});
            var Q60;
            {var subQ0=sQuery(id+"F0.wireOp",EDGE,"E39");Q60=makeQuery(id+"F0.imprint","IMPRINT",FACE,{"disambiguationData":[TD([[makeQuery(id+"F0.imprint","IMPRINT",EDGE,{"derivedFrom":subQ0}),-1.0]])]});}
            extrude(context, id + "F1", {"entities" : qUnion([Q0, Q1, Q2, Q3, Q4, Q5, Q6, Q7, Q8, Q9, Q10, Q11, Q12, Q13, Q14, Q15, Q16, Q17, Q18, Q19, Q20, Q21, Q22, Q23, Q24, Q25, Q26, Q27, Q28, Q29, Q30, Q31, Q32, Q33, Q34, Q35, Q36, Q37, Q38, Q39, Q40, Q41, Q42, Q43, Q44, Q45, Q46, Q47, Q48, Q49, Q50, Q51, Q52, Q53, Q54, Q55, Q56, Q57, Q58, Q59, Q60]), "oppositeDirection" : true, "depth" : 9 * mm});
        }
        {
            var Q0;
            {var subQ0=sQuery(id+"F0.wireOp",EDGE,"E39");Q0=makeQuery(id+"F0.imprint","IMPRINT",FACE,{"disambiguationData":[TD([[makeQuery(id+"F0.imprint","IMPRINT",EDGE,{"derivedFrom":subQ0}),-1.0]])]});}
            var Q1;
            {var subQ7=sQuery(id+"F0.wireOp",EDGE,"E33");Q1=makeQuery(id+"F0.imprint","IMPRINT",FACE,{"disambiguationData":[TD([[makeQuery(id+"F0.imprint","IMPRINT",EDGE,{"derivedFrom":subQ7}),-1.0]])]});}
            var Q2;
            {var subQ0=sQuery(id+"F0.wireOp",EDGE,"E41");Q2=makeQuery(id+"F0.imprint","IMPRINT",FACE,{"disambiguationData":[TD([[makeQuery(id+"F0.imprint","IMPRINT",EDGE,{"derivedFrom":subQ0}),-1.0]])]});}
            var Q3;
            {var subQ4=sQuery(id+"F0.wireOp",EDGE,"E35");Q3=makeQuery(id+"F0.imprint","IMPRINT",FACE,{"disambiguationData":[TD([[makeQuery(id+"F0.imprint","IMPRINT",EDGE,{"derivedFrom":subQ4}),1.0]])]});}
            var Q4;
            {var subQ0=sQuery(id+"F0.wireOp",EDGE,"E47");Q4=makeQuery(id+"F0.imprint","IMPRINT",FACE,{"disambiguationData":[TD([[makeQuery(id+"F0.imprint","IMPRINT",EDGE,{"derivedFrom":subQ0}),-1.0]])]});}
            var Q5;
            {var subQ0=sQuery(id+"F0.wireOp",EDGE,"E53");Q5=makeQuery(id+"F0.imprint","IMPRINT",FACE,{"disambiguationData":[TD([[makeQuery(id+"F0.imprint","IMPRINT",EDGE,{"derivedFrom":subQ0}),-1.0]])]});}
            var Q6;
            {var subQ0=sQuery(id+"F0.wireOp",EDGE,"E55");Q6=makeQuery(id+"F0.imprint","IMPRINT",FACE,{"disambiguationData":[TD([[makeQuery(id+"F0.imprint","IMPRINT",EDGE,{"derivedFrom":subQ0}),-1.0]])]});}
            var Q7;
            {var subQ3=sQuery(id+"F0.wireOp",EDGE,"E50");Q7=makeQuery(id+"F0.imprint","IMPRINT",FACE,{"disambiguationData":[TD([[makeQuery(id+"F0.imprint","IMPRINT",EDGE,{"derivedFrom":subQ3}),1.0]])]});}
            var Q8;
            {var subQ0=sQuery(id+"F0.wireOp",EDGE,"E66");Q8=makeQuery(id+"F0.imprint","IMPRINT",FACE,{"disambiguationData":[TD([[makeQuery(id+"F0.imprint","IMPRINT",EDGE,{"derivedFrom":subQ0}),-1.0]])]});}
            var Q9;
            {var subQ0=sQuery(id+"F0.wireOp",EDGE,"E64");Q9=makeQuery(id+"F0.imprint","IMPRINT",FACE,{"disambiguationData":[TD([[makeQuery(id+"F0.imprint","IMPRINT",EDGE,{"derivedFrom":subQ0}),-1.0]])]});}
            var Q10;
            {var subQ0=sQuery(id+"F0.wireOp",EDGE,"E90");Q10=makeQuery(id+"F0.imprint","IMPRINT",FACE,{"disambiguationData":[TD([[makeQuery(id+"F0.imprint","IMPRINT",EDGE,{"derivedFrom":subQ0}),-1.0]])]});}
            var Q11;
            {var subQ0=sQuery(id+"F0.wireOp",EDGE,"E92");Q11=makeQuery(id+"F0.imprint","IMPRINT",FACE,{"disambiguationData":[TD([[makeQuery(id+"F0.imprint","IMPRINT",EDGE,{"derivedFrom":subQ0}),-1.0]])]});}
            var Q12;
            {var subQ0=sQuery(id+"F0.wireOp",EDGE,"E94");Q12=makeQuery(id+"F0.imprint","IMPRINT",FACE,{"disambiguationData":[TD([[makeQuery(id+"F0.imprint","IMPRINT",EDGE,{"derivedFrom":subQ0}),-1.0]])]});}
            var Q13;
            Q13=makeQuery(id+"F0.imprint","IMPRINT",FACE,{"disambiguationData":[TD([[makeQuery(id+"F0.imprint","IMPRINT",EDGE,{"derivedFrom":sQuery(id+"F0.wireOp",EDGE,"E22.bottom")}),1.0]])]});
            var Q14;
            {var subQ0=sQuery(id+"F0.wireOp",EDGE,"E104");Q14=makeQuery(id+"F0.imprint","IMPRINT",FACE,{"disambiguationData":[TD([[makeQuery(id+"F0.imprint","IMPRINT",EDGE,{"derivedFrom":subQ0}),1.0]])]});}
            var Q15;
            {var subQ0=sQuery(id+"F0.wireOp",EDGE,"E105");Q15=makeQuery(id+"F0.imprint","IMPRINT",FACE,{"disambiguationData":[TD([[makeQuery(id+"F0.imprint","IMPRINT",EDGE,{"derivedFrom":subQ0}),-1.0]])]});}
            var Q16;
            Q16=makeQuery(id+"F0.imprint","IMPRINT",FACE,{"disambiguationData":[TD([[makeQuery(id+"F0.imprint","IMPRINT",EDGE,{"derivedFrom":sQuery(id+"F0.wireOp",EDGE,"E116")}),1.0]])]});
            var Q17;
            Q17=makeQuery(id+"F0.imprint","IMPRINT",FACE,{"disambiguationData":[TD([[makeQuery(id+"F0.imprint","IMPRINT",EDGE,{"derivedFrom":sQuery(id+"F0.wireOp",EDGE,"E119")}),-1.0]])]});
            var Q18;
            {var subQ5=sQuery(id+"F0.wireOp",EDGE,"E134");Q18=makeQuery(id+"F0.imprint","IMPRINT",FACE,{"disambiguationData":[TD([[makeQuery(id+"F0.imprint","IMPRINT",EDGE,{"derivedFrom":subQ5}),-1.0]])]});}
            var Q19;
            Q19=makeQuery(id+"F0.imprint","IMPRINT",FACE,{"disambiguationData":[TD([[makeQuery(id+"F0.imprint","IMPRINT",EDGE,{"derivedFrom":sQuery(id+"F0.wireOp",EDGE,"E145")}),1.0]])]});
            var Q20;
            Q20=makeQuery(id+"F0.imprint","IMPRINT",FACE,{"disambiguationData":[TD([[makeQuery(id+"F0.imprint","IMPRINT",EDGE,{"derivedFrom":sQuery(id+"F0.wireOp",EDGE,"E148")}),-1.0]])]});
            var Q21;
            {var subQ0=sQuery(id+"F0.wireOp",EDGE,"E135");Q21=makeQuery(id+"F0.imprint","IMPRINT",FACE,{"disambiguationData":[TD([[makeQuery(id+"F0.imprint","IMPRINT",EDGE,{"derivedFrom":subQ0}),-1.0]])]});}
            var Q22;
            {var subQ0=sQuery(id+"F0.wireOp",EDGE,"E139");Q22=makeQuery(id+"F0.imprint","IMPRINT",FACE,{"disambiguationData":[TD([[makeQuery(id+"F0.imprint","IMPRINT",EDGE,{"derivedFrom":subQ0}),-1.0]])]});}
            extrude(context, id + "F2", {"entities" : qUnion([Q0, Q1, Q2, Q3, Q4, Q5, Q6, Q7, Q8, Q9, Q10, Q11, Q12, Q13, Q14, Q15, Q16, Q17, Q18, Q19, Q20, Q21, Q22]), "operationType" : NewBodyOperationType.REMOVE, "oppositeDirection" : true, "depth" : 3 * mm});
        }
        {
            var Q0;
            Q0=qCreatedBy(makeId("Top.planeOp"),FACE);
            var sketch = newSketch(context, id + "F3", { "sketchPlane" : qUnion([Q0])});
            skLineSegment(sketch, "E154.0", {"start": v(-1685.91, 896.15) * mm, "end": v(2079.86, 896.15) * mm, "construction": true});
            skLineSegment(sketch, "E155", {"start": v(-249.8, 896.15) * mm, "end": v(-249.8, 864.15) * mm, "construction": true});
            skLineSegment(sketch, "E156", {"start": v(-249.8, 864.15) * mm, "end": v(-249.8, 849.15) * mm, "construction": true});
            skLineSegment(sketch, "E157", {"start": v(-249.8, 849.15) * mm, "end": v(2116.66, 849.15) * mm, "construction": true});
            skLineSegment(sketch, "E158.0", {"start": v(-154.73, 435.25) * mm, "end": v(-154.73, 1035.25) * mm, "construction": true});
            skLineSegment(sketch, "E159", {"start": v(-154.73, 778.4) * mm, "end": v(-122.73, 778.4) * mm, "construction": true});
            skLineSegment(sketch, "E160", {"start": v(-122.73, 778.4) * mm, "end": v(-122.73, 849.15) * mm, "construction": true});
            skCircle(sketch, "E161", {"center": v(-122.73, 849.15) * mm, "radius": 6 * mm});
            skCircle(sketch, "E162", {"center": v(-122.73, 849.15) * mm, "radius": 22.5 * mm, "construction": true});
            skLineSegment(sketch, "E163", {"start": v(-122.73, 808.5) * mm, "end": v(-122.73, 849.15) * mm, "construction": true});
            skLineSegment(sketch, "E164", {"start": v(-138.64, 865.06) * mm, "end": v(-122.73, 849.15) * mm, "construction": true});
            skLineSegment(sketch, "E165", {"start": v(-122.73, 849.15) * mm, "end": v(-106.82, 833.24) * mm, "construction": true});
            skCircle(sketch, "E166", {"center": v(-138.64, 865.06) * mm, "radius": 3.3 * mm});
            skCircle(sketch, "E167", {"center": v(-106.82, 833.24) * mm, "radius": 3.3 * mm});
            skLineSegment(sketch, "E168.0", {"start": v(392.07, 435.25) * mm, "end": v(392.07, 1035.25) * mm, "construction": true});
            skLineSegment(sketch, "E169", {"start": v(392.07, 833.43) * mm, "end": v(360.07, 833.43) * mm, "construction": true});
            skLineSegment(sketch, "E170", {"start": v(360.07, 833.43) * mm, "end": v(360.07, 849.15) * mm, "construction": true});
            skCircle(sketch, "E171", {"center": v(360.07, 849.15) * mm, "radius": 6 * mm});
            skCircle(sketch, "E172", {"center": v(360.07, 849.15) * mm, "radius": 22.5 * mm, "construction": true});
            skCircle(sketch, "E173", {"center": v(344.16, 833.24) * mm, "radius": 3.3 * mm});
            skCircle(sketch, "E174", {"center": v(375.98, 865.06) * mm, "radius": 3.3 * mm});
            skLineSegment(sketch, "E175", {"start": v(360.07, 849.15) * mm, "end": v(344.16, 833.24) * mm, "construction": true});
            skLineSegment(sketch, "E176", {"start": v(375.98, 865.06) * mm, "end": v(360.07, 849.15) * mm, "construction": true});
            skLineSegment(sketch, "E177", {"start": v(-138.64, 865.06) * mm, "end": v(-138.64, 849.15) * mm, "construction": true});
            skLineSegment(sketch, "E178", {"start": v(375.98, 865.06) * mm, "end": v(375.98, 849.15) * mm, "construction": true});
            skLineSegment(sketch, "E179.0", {"start": v(479.32, 435.25) * mm, "end": v(479.32, 1035.25) * mm, "construction": true});
            skLineSegment(sketch, "E180.0", {"start": v(1026.12, 435.25) * mm, "end": v(1026.12, 1035.25) * mm, "construction": true});
            skLineSegment(sketch, "E181", {"start": v(1112.16, 778.46) * mm, "end": v(1144.16, 778.46) * mm, "construction": true});
            skLineSegment(sketch, "E182", {"start": v(1144.16, 778.46) * mm, "end": v(1144.16, 864.15) * mm, "construction": true});
            skLineSegment(sketch, "E183", {"start": v(1451.16, 779.39) * mm, "end": v(1419.16, 779.39) * mm, "construction": true});
            skLineSegment(sketch, "E184", {"start": v(1419.16, 779.39) * mm, "end": v(1419.16, 864.15) * mm, "construction": true});
            skCircle(sketch, "E185", {"center": v(1144.16, 864.15) * mm, "radius": 6 * mm});
            skCircle(sketch, "E186", {"center": v(1419.16, 864.15) * mm, "radius": 6 * mm});
            skCircle(sketch, "E187", {"center": v(1144.16, 864.15) * mm, "radius": 22.5 * mm, "construction": true});
            skCircle(sketch, "E188", {"center": v(1160.07, 848.24) * mm, "radius": 3.3 * mm});
            skCircle(sketch, "E189", {"center": v(1128.25, 880.06) * mm, "radius": 3.3 * mm});
            skCircle(sketch, "E190", {"center": v(1419.16, 864.15) * mm, "radius": 22.5 * mm, "construction": true});
            skCircle(sketch, "E191", {"center": v(1435.07, 880.06) * mm, "radius": 3.3 * mm});
            skCircle(sketch, "E192", {"center": v(1403.25, 848.24) * mm, "radius": 3.3 * mm});
            skLineSegment(sketch, "E193", {"start": v(1160.07, 848.24) * mm, "end": v(1144.16, 864.15) * mm, "construction": true});
            skLineSegment(sketch, "E194", {"start": v(1144.16, 864.15) * mm, "end": v(1128.25, 880.06) * mm, "construction": true});
            skLineSegment(sketch, "E195", {"start": v(1435.07, 880.06) * mm, "end": v(1419.16, 864.15) * mm, "construction": true});
            skLineSegment(sketch, "E196", {"start": v(1419.16, 864.15) * mm, "end": v(1403.25, 848.24) * mm, "construction": true});
            skLineSegment(sketch, "E197.0", {"start": v(1454.16, 1035.25) * mm, "end": v(1454.16, 435.25) * mm, "construction": true});
            skLineSegment(sketch, "E198.0", {"start": v(1109.16, 435.25) * mm, "end": v(1109.16, 1035.25) * mm, "construction": true});
            skLineSegment(sketch, "E199", {"start": v(1451.16, 779.39) * mm, "end": v(1454.16, 779.39) * mm, "construction": true});
            skLineSegment(sketch, "E200", {"start": v(1109.16, 778.46) * mm, "end": v(1112.16, 778.46) * mm, "construction": true});
            skLineSegment(sketch, "E201", {"start": v(479.32, 777.65) * mm, "end": v(511.32, 777.65) * mm, "construction": true});
            skLineSegment(sketch, "E202", {"start": v(511.32, 777.65) * mm, "end": v(511.32, 849.15) * mm, "construction": true});
            skCircle(sketch, "E203", {"center": v(511.32, 849.15) * mm, "radius": 22.5 * mm, "construction": true});
            skCircle(sketch, "E204", {"center": v(495.41, 865.06) * mm, "radius": 3.3 * mm});
            skCircle(sketch, "E205", {"center": v(527.23, 833.24) * mm, "radius": 3.3 * mm});
            skCircle(sketch, "E206", {"center": v(511.32, 849.15) * mm, "radius": 6 * mm});
            skLineSegment(sketch, "E207", {"start": v(495.41, 865.06) * mm, "end": v(511.32, 849.15) * mm, "construction": true});
            skLineSegment(sketch, "E208", {"start": v(527.23, 833.24) * mm, "end": v(511.32, 849.15) * mm, "construction": true});
            skLineSegment(sketch, "E209", {"start": v(994.12, 820.6) * mm, "end": v(994.12, 849.15) * mm, "construction": true});
            skCircle(sketch, "E210", {"center": v(994.12, 849.15) * mm, "radius": 22.5 * mm, "construction": true});
            skCircle(sketch, "E211", {"center": v(1010.03, 865.06) * mm, "radius": 3.3 * mm});
            skCircle(sketch, "E212", {"center": v(978.21, 833.24) * mm, "radius": 3.3 * mm});
            skCircle(sketch, "E213", {"center": v(994.12, 849.15) * mm, "radius": 6 * mm});
            skLineSegment(sketch, "E214", {"start": v(1010.03, 865.06) * mm, "end": v(994.12, 849.15) * mm, "construction": true});
            skLineSegment(sketch, "E215", {"start": v(978.21, 833.24) * mm, "end": v(994.12, 849.15) * mm, "construction": true});
            skLineSegment(sketch, "E216", {"start": v(1010.03, 865.06) * mm, "end": v(1010.03, 849.15) * mm, "construction": true});
            skLineSegment(sketch, "E217", {"start": v(994.12, 820.6) * mm, "end": v(1026.12, 820.6) * mm, "construction": true});
            skLineSegment(sketch, "E218", {"start": v(-249.8, 864.15) * mm, "end": v(2099.82, 864.15) * mm, "construction": true});
            skCircle(sketch, "E219", {"center": v(-122.73, 849.15) * mm, "radius": 17.5 * mm});
            skCircle(sketch, "E220", {"center": v(360.07, 849.15) * mm, "radius": 17.5 * mm});
            skCircle(sketch, "E221", {"center": v(511.32, 849.15) * mm, "radius": 17.5 * mm});
            skCircle(sketch, "E222", {"center": v(994.12, 849.15) * mm, "radius": 17.5 * mm});
            skCircle(sketch, "E223", {"center": v(1144.16, 864.15) * mm, "radius": 17.5 * mm});
            skCircle(sketch, "E224", {"center": v(1419.16, 864.15) * mm, "radius": 17.5 * mm});
            skLineSegment(sketch, "E225", {"start": v(-157.73, 128.42) * mm, "end": v(395.07, 128.42) * mm, "construction": true});
            skLineSegment(sketch, "E226", {"start": v(-157.73, 128.42) * mm, "end": v(-134.73, 128.42) * mm, "construction": true});
            skLineSegment(sketch, "E227", {"start": v(-134.73, 128.42) * mm, "end": v(-134.73, 198.42) * mm, "construction": true});
            skLineSegment(sketch, "E228", {"start": v(-134.73, 128.42) * mm, "end": v(-134.73, 58.42) * mm, "construction": true});
            skLineSegment(sketch, "E229", {"start": v(395.07, 128.42) * mm, "end": v(375.07, 128.42) * mm, "construction": true});
            skLineSegment(sketch, "E230", {"start": v(375.07, 128.42) * mm, "end": v(375.07, 198.42) * mm, "construction": true});
            skLineSegment(sketch, "E231", {"start": v(375.07, 128.42) * mm, "end": v(375.07, 58.42) * mm, "construction": true});
            skCircle(sketch, "E232", {"center": v(-134.73, 198.42) * mm, "radius": 5 * mm});
            skCircle(sketch, "E233", {"center": v(-134.73, 58.42) * mm, "radius": 5 * mm});
            skCircle(sketch, "E234", {"center": v(375.07, 198.42) * mm, "radius": 5 * mm});
            skCircle(sketch, "E235", {"center": v(375.07, 58.42) * mm, "radius": 5 * mm});
            skLineSegment(sketch, "E236.0", {"start": v(395.07, -88.27) * mm, "end": v(395.07, -433.27) * mm, "construction": true});
            skLineSegment(sketch, "E237", {"start": v(403.63, -260.77) * mm, "end": v(-119.73, -260.77) * mm, "construction": true});
            skLineSegment(sketch, "E238.0", {"start": v(-157.73, -88.27) * mm, "end": v(-157.73, -433.27) * mm, "construction": true});
            skLineSegment(sketch, "E239", {"start": v(-134.73, 58.42) * mm, "end": v(-134.73, -435.33) * mm, "construction": true});
            skLineSegment(sketch, "E240", {"start": v(375.07, 58.42) * mm, "end": v(375.07, -442.17) * mm, "construction": true});
            skCircle(sketch, "E241", {"center": v(-134.73, -248.27) * mm, "radius": 70 * mm, "construction": true});
            skCircle(sketch, "E242", {"center": v(375.07, -248.27) * mm, "radius": 70 * mm, "construction": true});
            skCircle(sketch, "E243", {"center": v(-134.73, -178.27) * mm, "radius": 5 * mm});
            skPoint(sketch, "E243.centerSnap0", {"position": v(-134.73, -188.45) * mm});
            skCircle(sketch, "E244", {"center": v(-134.73, -318.27) * mm, "radius": 5 * mm});
            skCircle(sketch, "E245", {"center": v(375.07, -178.27) * mm, "radius": 5 * mm});
            skCircle(sketch, "E246", {"center": v(375.07, -318.27) * mm, "radius": 5 * mm});
            skLineSegment(sketch, "E247", {"start": v(-134.73, -248.27) * mm, "end": v(375.07, -248.27) * mm, "construction": true});
            skLineSegment(sketch, "E248.0", {"start": v(-157.73, -433.27) * mm, "end": v(395.07, -433.27) * mm, "construction": true});
            skLineSegment(sketch, "E249", {"start": v(174.89, -433.27) * mm, "end": v(174.89, -248.27) * mm, "construction": true});
            skCircle(sketch, "E250", {"center": v(375.07, 128.42) * mm, "radius": 18.25 * mm, "construction": true});
            skCircle(sketch, "E251", {"center": v(-134.73, 128.42) * mm, "radius": 18.25 * mm, "construction": true});
            skCircle(sketch, "E252", {"center": v(-134.73, -248.27) * mm, "radius": 18.25 * mm, "construction": true});
            skCircle(sketch, "E253", {"center": v(375.07, -248.27) * mm, "radius": 18.25 * mm, "construction": true});
            skCircle(sketch, "E254", {"center": v(-134.73, 128.42) * mm, "radius": 4.25 * mm});
            skCircle(sketch, "E255", {"center": v(375.07, 128.42) * mm, "radius": 4.25 * mm});
            skCircle(sketch, "E256", {"center": v(375.07, -248.27) * mm, "radius": 4.25 * mm});
            skCircle(sketch, "E257", {"center": v(-134.73, -248.27) * mm, "radius": 4.25 * mm});
            skCircle(sketch, "E258", {"center": v(-134.73, -230.02) * mm, "radius": 2.5 * mm});
            skCircle(sketch, "E259", {"center": v(-134.73, -266.52) * mm, "radius": 2.5 * mm});
            skCircle(sketch, "E260", {"center": v(375.07, -230.02) * mm, "radius": 2.5 * mm});
            skCircle(sketch, "E261", {"center": v(375.07, -266.52) * mm, "radius": 2.5 * mm});
            skCircle(sketch, "E262", {"center": v(375.07, 146.67) * mm, "radius": 2.5 * mm});
            skCircle(sketch, "E263", {"center": v(375.07, 110.17) * mm, "radius": 2.5 * mm});
            skCircle(sketch, "E264", {"center": v(-134.73, 146.67) * mm, "radius": 2.5 * mm});
            skCircle(sketch, "E265", {"center": v(-134.73, 110.17) * mm, "radius": 2.5 * mm});
            skCircle(sketch, "E266", {"center": v(-397.55, 636.07) * mm, "radius": 21.9 * mm, "construction": true});
            skLineSegment(sketch, "E267", {"start": v(-413.03, 651.56) * mm, "end": v(-382.06, 620.59) * mm, "construction": true});
            skLineSegment(sketch, "E268", {"start": v(-382.06, 651.56) * mm, "end": v(-413.03, 620.59) * mm, "construction": true});
            skCircle(sketch, "E269", {"center": v(-413.03, 651.56) * mm, "radius": 1.5 * mm});
            skCircle(sketch, "E270", {"center": v(-382.06, 651.56) * mm, "radius": 1.5 * mm});
            skCircle(sketch, "E271", {"center": v(-382.06, 620.59) * mm, "radius": 1.5 * mm});
            skCircle(sketch, "E272", {"center": v(-413.03, 620.59) * mm, "radius": 1.5 * mm});
            skLineSegment(sketch, "E273", {"start": v(-397.55, 657.97) * mm, "end": v(-397.55, 614.17) * mm, "construction": true});
            skCircle(sketch, "E274", {"center": v(360.07, 849.15) * mm, "radius": 21.9 * mm, "construction": true});
            skLineSegment(sketch, "E275", {"start": v(360.07, 871.05) * mm, "end": v(360.07, 827.25) * mm, "construction": true});
            skLineSegment(sketch, "E276", {"start": v(381.97, 849.15) * mm, "end": v(338.17, 849.15) * mm, "construction": true});
            skCircle(sketch, "E277", {"center": v(360.07, 871.05) * mm, "radius": 1.5 * mm});
            skCircle(sketch, "E278", {"center": v(381.97, 849.15) * mm, "radius": 1.5 * mm});
            skCircle(sketch, "E279", {"center": v(360.07, 827.25) * mm, "radius": 1.5 * mm});
            skCircle(sketch, "E280", {"center": v(338.17, 849.15) * mm, "radius": 1.5 * mm});
            skCircle(sketch, "E281", {"center": v(1144.16, 864.15) * mm, "radius": 21.9 * mm, "construction": true});
            skLineSegment(sketch, "E282", {"start": v(1144.16, 886.05) * mm, "end": v(1144.16, 842.25) * mm, "construction": true});
            skLineSegment(sketch, "E283", {"start": v(1166.06, 864.15) * mm, "end": v(1122.26, 864.15) * mm, "construction": true});
            skCircle(sketch, "E284", {"center": v(1144.16, 886.05) * mm, "radius": 1.5 * mm});
            skCircle(sketch, "E285", {"center": v(1166.06, 864.15) * mm, "radius": 1.5 * mm});
            skCircle(sketch, "E286", {"center": v(1144.16, 842.25) * mm, "radius": 1.5 * mm});
            skCircle(sketch, "E287", {"center": v(1122.26, 864.15) * mm, "radius": 1.5 * mm});
            skCircle(sketch, "E288", {"center": v(-134.73, 128.42) * mm, "radius": 21.9 * mm, "construction": true});
            skLineSegment(sketch, "E289", {"start": v(-150.22, 143.9) * mm, "end": v(-119.25, 112.93) * mm, "construction": true});
            skLineSegment(sketch, "E290", {"start": v(-119.25, 143.9) * mm, "end": v(-150.22, 112.93) * mm, "construction": true});
            skCircle(sketch, "E291", {"center": v(-150.22, 143.9) * mm, "radius": 1.5 * mm});
            skCircle(sketch, "E292", {"center": v(-119.25, 143.9) * mm, "radius": 1.5 * mm});
            skCircle(sketch, "E293", {"center": v(-119.25, 112.93) * mm, "radius": 1.5 * mm});
            skCircle(sketch, "E294", {"center": v(-150.22, 112.93) * mm, "radius": 1.5 * mm});
            skLineSegment(sketch, "E295", {"start": v(-134.73, 150.32) * mm, "end": v(-134.73, 106.52) * mm, "construction": true});
            skCircle(sketch, "E296", {"center": v(375.07, 128.42) * mm, "radius": 21.9 * mm, "construction": true});
            skLineSegment(sketch, "E297", {"start": v(359.58, 143.9) * mm, "end": v(390.55, 112.93) * mm, "construction": true});
            skLineSegment(sketch, "E298", {"start": v(390.55, 143.9) * mm, "end": v(359.58, 112.93) * mm, "construction": true});
            skCircle(sketch, "E299", {"center": v(359.58, 143.9) * mm, "radius": 1.5 * mm});
            skCircle(sketch, "E300", {"center": v(390.55, 143.9) * mm, "radius": 1.5 * mm});
            skCircle(sketch, "E301", {"center": v(390.55, 112.93) * mm, "radius": 1.5 * mm});
            skCircle(sketch, "E302", {"center": v(359.58, 112.93) * mm, "radius": 1.5 * mm});
            skLineSegment(sketch, "E303", {"start": v(375.07, 150.32) * mm, "end": v(375.07, 106.52) * mm, "construction": true});
            skLineSegment(sketch, "E304", {"start": v(1889.54, 791.9) * mm, "end": v(1857.54, 791.9) * mm, "construction": true});
            skLineSegment(sketch, "E305", {"start": v(1857.54, 791.9) * mm, "end": v(1857.54, 864.15) * mm, "construction": true});
            skCircle(sketch, "E306", {"center": v(1857.54, 864.15) * mm, "radius": 6 * mm});
            skCircle(sketch, "E307", {"center": v(1857.54, 864.15) * mm, "radius": 22.5 * mm, "construction": true});
            skCircle(sketch, "E308", {"center": v(1873.45, 880.06) * mm, "radius": 3.3 * mm});
            skCircle(sketch, "E309", {"center": v(1841.63, 848.24) * mm, "radius": 3.3 * mm});
            skLineSegment(sketch, "E310", {"start": v(1873.45, 880.06) * mm, "end": v(1857.54, 864.15) * mm, "construction": true});
            skLineSegment(sketch, "E311", {"start": v(1857.54, 864.15) * mm, "end": v(1841.63, 848.24) * mm, "construction": true});
            skLineSegment(sketch, "E312", {"start": v(1889.54, 791.9) * mm, "end": v(1892.54, 791.9) * mm, "construction": true});
            skCircle(sketch, "E313", {"center": v(1857.54, 864.15) * mm, "radius": 17.5 * mm});
            skLineSegment(sketch, "E314", {"start": v(1582.54, 779.15) * mm, "end": v(1550.54, 779.15) * mm, "construction": true});
            skLineSegment(sketch, "E315", {"start": v(1582.54, 779.15) * mm, "end": v(1582.54, 864.15) * mm, "construction": true});
            skCircle(sketch, "E316", {"center": v(1582.54, 864.15) * mm, "radius": 6 * mm});
            skCircle(sketch, "E317", {"center": v(1582.54, 864.15) * mm, "radius": 22.5 * mm, "construction": true});
            skCircle(sketch, "E318", {"center": v(1566.63, 880.06) * mm, "radius": 3.3 * mm});
            skCircle(sketch, "E319", {"center": v(1598.45, 848.24) * mm, "radius": 3.3 * mm});
            skLineSegment(sketch, "E320", {"start": v(1566.63, 880.06) * mm, "end": v(1582.54, 864.15) * mm, "construction": true});
            skLineSegment(sketch, "E321", {"start": v(1582.54, 864.15) * mm, "end": v(1598.45, 848.24) * mm, "construction": true});
            skLineSegment(sketch, "E322", {"start": v(1547.54, 779.15) * mm, "end": v(1550.54, 779.15) * mm, "construction": true});
            skCircle(sketch, "E323", {"center": v(1582.54, 864.15) * mm, "radius": 17.5 * mm});
            skLineSegment(sketch, "E324", {"start": v(495.41, 865.06) * mm, "end": v(495.41, 849.15) * mm, "construction": true});
            skSolve(sketch);
        }
        {
            var Q0;
            Q0 = qSketchRegion(id + "F3", true);
            var Q1;
            Q1=makeQuery(id+"F3.imprint","IMPRINT",FACE,{"disambiguationData":[TD([[makeQuery(id+"F3.imprint","IMPRINT",EDGE,{"derivedFrom":sQuery(id+"F3.wireOp",EDGE,"E161")}),1.0]])]});
            var Q2;
            Q2=makeQuery(id+"F3.imprint","IMPRINT",FACE,{"disambiguationData":[TD([[makeQuery(id+"F3.imprint","IMPRINT",EDGE,{"derivedFrom":sQuery(id+"F3.wireOp",EDGE,"E171")}),1.0]])]});
            var Q3;
            Q3=makeQuery(id+"F3.imprint","IMPRINT",FACE,{"disambiguationData":[TD([[makeQuery(id+"F3.imprint","IMPRINT",EDGE,{"derivedFrom":sQuery(id+"F3.wireOp",EDGE,"E206")}),1.0]])]});
            var Q4;
            Q4=makeQuery(id+"F3.imprint","IMPRINT",FACE,{"disambiguationData":[TD([[makeQuery(id+"F3.imprint","IMPRINT",EDGE,{"derivedFrom":sQuery(id+"F3.wireOp",EDGE,"E213")}),1.0]])]});
            var Q5;
            Q5=makeQuery(id+"F3.imprint","IMPRINT",FACE,{"disambiguationData":[TD([[makeQuery(id+"F3.imprint","IMPRINT",EDGE,{"derivedFrom":sQuery(id+"F3.wireOp",EDGE,"E186")}),1.0]])]});
            var Q6;
            Q6=makeQuery(id+"F3.imprint","IMPRINT",FACE,{"disambiguationData":[TD([[makeQuery(id+"F3.imprint","IMPRINT",EDGE,{"derivedFrom":sQuery(id+"F3.wireOp",EDGE,"E185")}),1.0]])]});
            var Q7;
            Q7=makeQuery(id+"F3.imprint","IMPRINT",FACE,{"disambiguationData":[TD([[makeQuery(id+"F3.imprint","IMPRINT",EDGE,{"derivedFrom":sQuery(id+"F3.wireOp",EDGE,"E316")}),1.0]])]});
            var Q8;
            Q8=makeQuery(id+"F3.imprint","IMPRINT",FACE,{"disambiguationData":[TD([[makeQuery(id+"F3.imprint","IMPRINT",EDGE,{"derivedFrom":sQuery(id+"F3.wireOp",EDGE,"E306")}),1.0]])]});
            extrude(context, id + "F4", {"entities" : qUnion([Q0, Q1, Q2, Q3, Q4, Q5, Q6, Q7, Q8]), "operationType" : NewBodyOperationType.REMOVE, "oppositeDirection" : true, "depth" : 16.75 * mm});
        }
        {
            var Q0;
            Q0=qCreatedBy(makeId("Top.planeOp"),FACE);
            var sketch = newSketch(context, id + "F5", { "sketchPlane" : qUnion([Q0])});
            skLineSegment(sketch, "E325.bottom", {"start": v(2409.57, 776.86) * mm, "end": v(3009.57, 776.86) * mm});
            skLineSegment(sketch, "E325.top", {"start": v(2409.57, -423.14) * mm, "end": v(3009.57, -423.14) * mm});
            skLineSegment(sketch, "E325.left", {"start": v(2409.57, 776.86) * mm, "end": v(2409.57, -423.14) * mm});
            skLineSegment(sketch, "E325.right", {"start": v(3009.57, 776.86) * mm, "end": v(3009.57, -423.14) * mm});
            skLineSegment(sketch, "E326.bottom", {"start": v(3111.28, 771.2) * mm, "end": v(3711.28, 771.2) * mm});
            skLineSegment(sketch, "E326.top", {"start": v(3111.28, -428.8) * mm, "end": v(3711.28, -428.8) * mm});
            skLineSegment(sketch, "E326.left", {"start": v(3111.28, 771.2) * mm, "end": v(3111.28, -428.8) * mm});
            skLineSegment(sketch, "E326.right", {"start": v(3711.28, 771.2) * mm, "end": v(3711.28, -428.8) * mm});
            skSolve(sketch);
        }
        {
            var Q0;
            Q0 = qSketchRegion(id + "F5", true);
            extrude(context, id + "F6", {"entities" : qUnion([Q0]), "depth" : 6 * mm});
        }
        {
            var Q0;
            Q0=makeQuery(id+"F1.opExtrude","SWEPT_EDGE",EDGE,{"disambiguationData":[OSD([sQuery(id+"F0.wireOp",EDGE,"E0"),sQuery(id+"F0.wireOp",EDGE,"E1")])]});
            var Q1;
            Q1=makeQuery(id+"F1.opExtrude","SWEPT_EDGE",EDGE,{"disambiguationData":[OSD([sQuery(id+"F0.wireOp",EDGE,"E1"),sQuery(id+"F0.wireOp",EDGE,"E2")])]});
            var Q2;
            Q2=makeQuery(id+"F1.opExtrude","SWEPT_EDGE",EDGE,{"disambiguationData":[OSD([sQuery(id+"F0.wireOp",EDGE,"E12"),sQuery(id+"F0.wireOp",EDGE,"E13")])]});
            var Q3;
            Q3=makeQuery(id+"F1.opExtrude","SWEPT_EDGE",EDGE,{"disambiguationData":[OSD([sQuery(id+"F0.wireOp",EDGE,"E11"),sQuery(id+"F0.wireOp",EDGE,"E12")])]});
            var Q4;
            Q4=makeQuery(id+"F1.opExtrude","SWEPT_EDGE",EDGE,{"disambiguationData":[OSD([sQuery(id+"F0.wireOp",EDGE,"E29"),sQuery(id+"F0.wireOp",EDGE,"E30")])]});
            var Q5;
            Q5=makeQuery(id+"F1.opExtrude","SWEPT_EDGE",EDGE,{"disambiguationData":[OSD([sQuery(id+"F0.wireOp",EDGE,"E28"),sQuery(id+"F0.wireOp",EDGE,"E29")])]});
            var Q6;
            Q6=makeQuery(id+"F1.opExtrude","SWEPT_EDGE",EDGE,{"disambiguationData":[OSD([sQuery(id+"F0.wireOp",EDGE,"E129"),sQuery(id+"F0.wireOp",EDGE,"E130")])]});
            var Q7;
            Q7=makeQuery(id+"F1.opExtrude","SWEPT_EDGE",EDGE,{"disambiguationData":[OSD([sQuery(id+"F0.wireOp",EDGE,"E128"),sQuery(id+"F0.wireOp",EDGE,"E129")])]});
            fillet(context, id + "F7", {"entities" : qUnion([Q0, Q1, Q2, Q3, Q4, Q5, Q6, Q7]), "radius" : 94.76 * mm, "tangentPropagation" : true, "allowEdgeOverflow" : false});
        }
        {
            var Q0;
            Q0=makeQuery(id+"F1.opExtrude","SWEPT_EDGE",EDGE,{"disambiguationData":[OSD([sQuery(id+"F0.wireOp",EDGE,"E5"),sQuery(id+"F0.wireOp",EDGE,"E6")])]});
            var Q1;
            Q1=makeQuery(id+"F1.opExtrude","SWEPT_EDGE",EDGE,{"disambiguationData":[OSD([sQuery(id+"F0.wireOp",EDGE,"E6"),sQuery(id+"F0.wireOp",EDGE,"E7")])]});
            var Q2;
            Q2=makeQuery(id+"F1.opExtrude","SWEPT_EDGE",EDGE,{"disambiguationData":[OSD([sQuery(id+"F0.wireOp",EDGE,"E8"),sQuery(id+"F0.wireOp",EDGE,"E15")])]});
            var Q3;
            Q3=makeQuery(id+"F1.opExtrude","SWEPT_EDGE",EDGE,{"disambiguationData":[OSD([sQuery(id+"F0.wireOp",EDGE,"E8"),sQuery(id+"F0.wireOp",EDGE,"E9")])]});
            var Q4;
            Q4=makeQuery(id+"F1.opExtrude","SWEPT_EDGE",EDGE,{"disambiguationData":[OSD([sQuery(id+"F0.wireOp",EDGE,"E9"),sQuery(id+"F0.wireOp",EDGE,"E10")])]});
            var Q5;
            Q5=makeQuery(id+"F7.opFillet","BLEND_EDGE",EDGE,{"blendedFrom":[makeQuery(id+"F1.opExtrude","SWEPT_EDGE",EDGE,{"disambiguationData":[OSD([sQuery(id+"F0.wireOp",EDGE,"E11"),sQuery(id+"F0.wireOp",EDGE,"E12")])]}),makeQuery(id+"F1.opExtrude","SWEPT_FACE",FACE,{"disambiguationData":[OSD([sQuery(id+"F0.wireOp",EDGE,"E10")])]})],"blendedInto":[makeQuery(id+"F1.opExtrude","SWEPT_FACE",FACE,{"disambiguationData":[OSD([sQuery(id+"F0.wireOp",EDGE,"E10")])]})]});
            var Q6;
            Q6=makeQuery(id+"F1.opExtrude","SWEPT_EDGE",EDGE,{"disambiguationData":[OSD([sQuery(id+"F0.wireOp",EDGE,"E14"),sQuery(id+"F0.wireOp",EDGE,"E15")])]});
            var Q7;
            Q7=makeQuery(id+"F7.opFillet","BLEND_EDGE",EDGE,{"blendedFrom":[makeQuery(id+"F1.opExtrude","SWEPT_EDGE",EDGE,{"disambiguationData":[OSD([sQuery(id+"F0.wireOp",EDGE,"E12"),sQuery(id+"F0.wireOp",EDGE,"E13")])]}),makeQuery(id+"F1.opExtrude","SWEPT_FACE",FACE,{"disambiguationData":[OSD([sQuery(id+"F0.wireOp",EDGE,"E14")])]})],"blendedInto":[makeQuery(id+"F1.opExtrude","SWEPT_FACE",FACE,{"disambiguationData":[OSD([sQuery(id+"F0.wireOp",EDGE,"E14")])]})]});
            var Q8;
            Q8=makeQuery(id+"F1.opExtrude","SWEPT_EDGE",EDGE,{"disambiguationData":[OSD([sQuery(id+"F0.wireOp",EDGE,"E3"),sQuery(id+"F0.wireOp",EDGE,"E7")])]});
            var Q9;
            Q9=makeQuery(id+"F7.opFillet","BLEND_EDGE",EDGE,{"blendedFrom":[makeQuery(id+"F1.opExtrude","SWEPT_EDGE",EDGE,{"disambiguationData":[OSD([sQuery(id+"F0.wireOp",EDGE,"E1"),sQuery(id+"F0.wireOp",EDGE,"E2")])]}),makeQuery(id+"F1.opExtrude","SWEPT_FACE",FACE,{"disambiguationData":[OSD([sQuery(id+"F0.wireOp",EDGE,"E3")])]})],"blendedInto":[makeQuery(id+"F1.opExtrude","SWEPT_FACE",FACE,{"disambiguationData":[OSD([sQuery(id+"F0.wireOp",EDGE,"E3")])]})]});
            var Q10;
            Q10=makeQuery(id+"F1.opExtrude","SWEPT_EDGE",EDGE,{"disambiguationData":[OSD([sQuery(id+"F0.wireOp",EDGE,"E4"),sQuery(id+"F0.wireOp",EDGE,"E5")])]});
            var Q11;
            Q11=makeQuery(id+"F7.opFillet","BLEND_EDGE",EDGE,{"blendedFrom":[makeQuery(id+"F1.opExtrude","SWEPT_EDGE",EDGE,{"disambiguationData":[OSD([sQuery(id+"F0.wireOp",EDGE,"E0"),sQuery(id+"F0.wireOp",EDGE,"E1")])]}),makeQuery(id+"F1.opExtrude","SWEPT_FACE",FACE,{"disambiguationData":[OSD([sQuery(id+"F0.wireOp",EDGE,"E4")])]})],"blendedInto":[makeQuery(id+"F1.opExtrude","SWEPT_FACE",FACE,{"disambiguationData":[OSD([sQuery(id+"F0.wireOp",EDGE,"E4")])]})]});
            var Q12;
            Q12=makeQuery(id+"F7.opFillet","BLEND_EDGE",EDGE,{"blendedFrom":[makeQuery(id+"F1.opExtrude","SWEPT_EDGE",EDGE,{"disambiguationData":[OSD([sQuery(id+"F0.wireOp",EDGE,"E29"),sQuery(id+"F0.wireOp",EDGE,"E30")])]}),makeQuery(id+"F1.opExtrude","SWEPT_FACE",FACE,{"disambiguationData":[OSD([sQuery(id+"F0.wireOp",EDGE,"E31")])]})],"blendedInto":[makeQuery(id+"F1.opExtrude","SWEPT_FACE",FACE,{"disambiguationData":[OSD([sQuery(id+"F0.wireOp",EDGE,"E31")])]})]});
            var Q13;
            Q13=makeQuery(id+"F7.opFillet","BLEND_EDGE",EDGE,{"blendedFrom":[makeQuery(id+"F1.opExtrude","SWEPT_EDGE",EDGE,{"disambiguationData":[OSD([sQuery(id+"F0.wireOp",EDGE,"E28"),sQuery(id+"F0.wireOp",EDGE,"E29")])]}),makeQuery(id+"F1.opExtrude","SWEPT_FACE",FACE,{"disambiguationData":[OSD([sQuery(id+"F0.wireOp",EDGE,"E27")])]})],"blendedInto":[makeQuery(id+"F1.opExtrude","SWEPT_FACE",FACE,{"disambiguationData":[OSD([sQuery(id+"F0.wireOp",EDGE,"E27")])]})]});
            var Q14;
            Q14=makeQuery(id+"F7.opFillet","BLEND_EDGE",EDGE,{"blendedFrom":[makeQuery(id+"F1.opExtrude","SWEPT_EDGE",EDGE,{"disambiguationData":[OSD([sQuery(id+"F0.wireOp",EDGE,"E129"),sQuery(id+"F0.wireOp",EDGE,"E130")])]}),makeQuery(id+"F1.opExtrude","SWEPT_FACE",FACE,{"disambiguationData":[OSD([sQuery(id+"F0.wireOp",EDGE,"E131")])]})],"blendedInto":[makeQuery(id+"F1.opExtrude","SWEPT_FACE",FACE,{"disambiguationData":[OSD([sQuery(id+"F0.wireOp",EDGE,"E131")])]})]});
            var Q15;
            Q15=makeQuery(id+"F7.opFillet","BLEND_EDGE",EDGE,{"blendedFrom":[makeQuery(id+"F1.opExtrude","SWEPT_EDGE",EDGE,{"disambiguationData":[OSD([sQuery(id+"F0.wireOp",EDGE,"E128"),sQuery(id+"F0.wireOp",EDGE,"E129")])]}),makeQuery(id+"F1.opExtrude","SWEPT_FACE",FACE,{"disambiguationData":[OSD([sQuery(id+"F0.wireOp",EDGE,"E127")])]})],"blendedInto":[makeQuery(id+"F1.opExtrude","SWEPT_FACE",FACE,{"disambiguationData":[OSD([sQuery(id+"F0.wireOp",EDGE,"E127")])]})]});
            fillet(context, id + "F8", {"entities" : qUnion([Q0, Q1, Q2, Q3, Q4, Q5, Q6, Q7, Q8, Q9, Q10, Q11, Q12, Q13, Q14, Q15]), "radius" : 5 * mm, "tangentPropagation" : true, "allowEdgeOverflow" : false});
        }
    });
